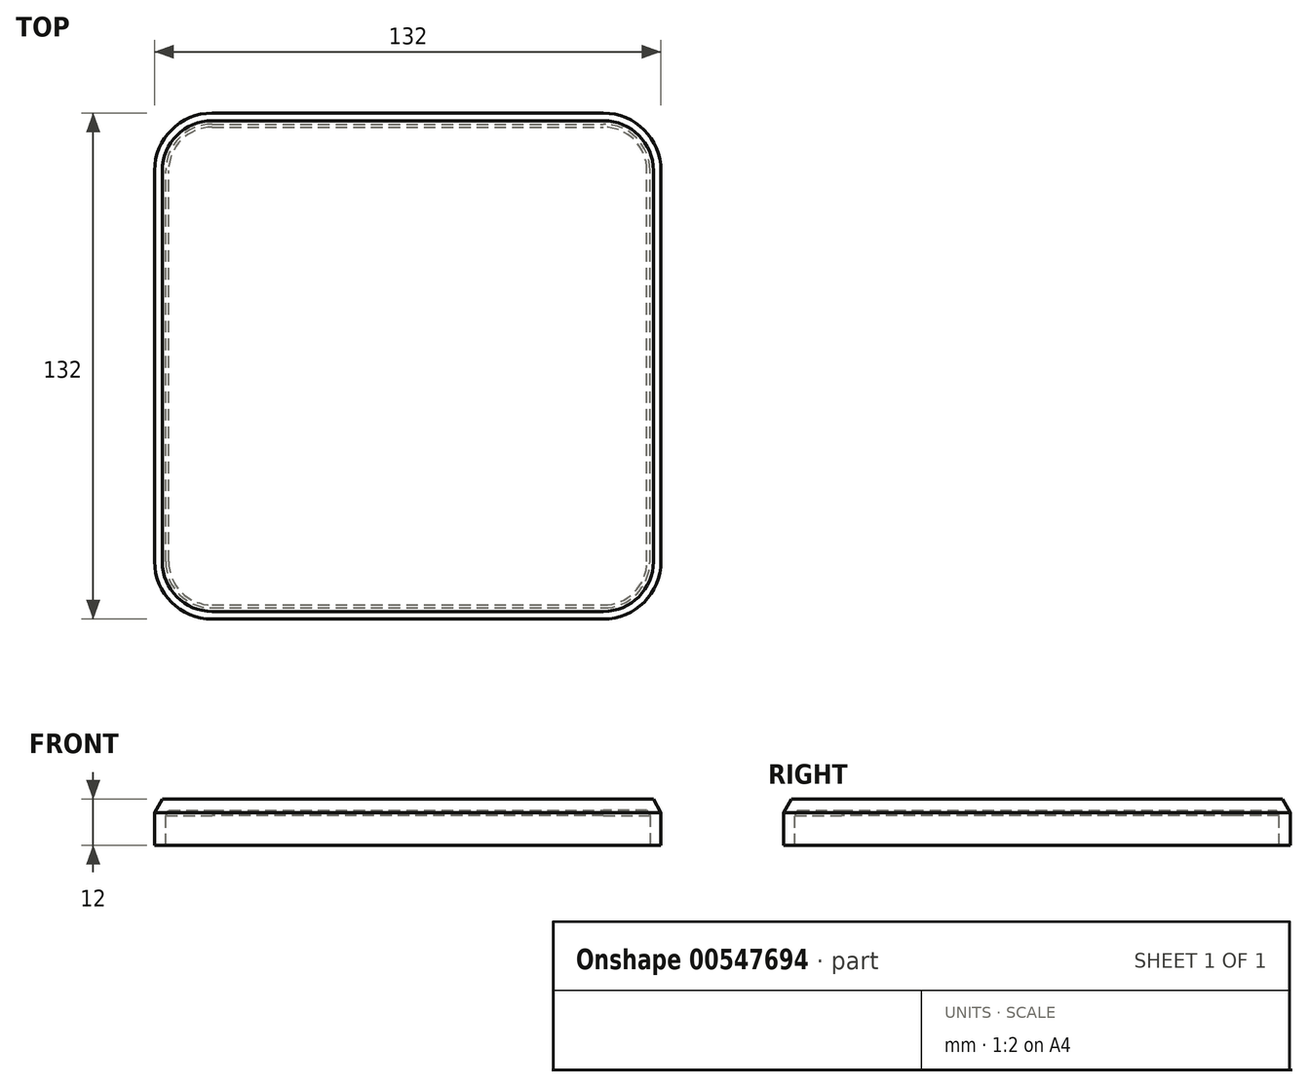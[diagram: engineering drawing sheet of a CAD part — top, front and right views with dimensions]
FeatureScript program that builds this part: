
annotation { "Feature Type Name" : "Feature", "Feature Type Description" : "" }
export const myFeature = defineFeature(function(context is Context, id is Id, definition is map)
    precondition{}
    {
        {
            var Q0;
            Q0=qCreatedBy(makeId("Top.planeOp"),FACE);
            var sketch = newSketch(context, id + "F0", { "sketchPlane" : qUnion([Q0])});
            skLineSegment(sketch, "E0.bottom", {"start": v(-51, -66) * mm, "end": v(51, -66) * mm});
            skLineSegment(sketch, "E0.top", {"start": v(-51, 66) * mm, "end": v(51, 66) * mm});
            skLineSegment(sketch, "E0.left", {"start": v(-66, -51) * mm, "end": v(-66, 51) * mm});
            skLineSegment(sketch, "E0.right", {"start": v(66, -51) * mm, "end": v(66, 51) * mm});
            skPoint(sketch, "E1", {"position": v(-66, 0) * mm});
            skPoint(sketch, "E2", {"position": v(0, 66) * mm});
            skPoint(sketch, "E3.visualSharp", {"position": v(-66, 66) * mm});
            skArc(sketch, "E3.filletArc", {"start": v(-51, 66) * mm, "mid": v(-61.6, 61.6) * mm, "end": v(-66, 51) * mm});
            skPoint(sketch, "E4.visualSharp", {"position": v(66, 66) * mm});
            skArc(sketch, "E4.filletArc", {"start": v(66, 51) * mm, "mid": v(61.6, 61.6) * mm, "end": v(51, 66) * mm});
            skPoint(sketch, "E5.visualSharp", {"position": v(66, -66) * mm});
            skArc(sketch, "E5.filletArc", {"start": v(51, -66) * mm, "mid": v(61.6, -61.6) * mm, "end": v(66, -51) * mm});
            skPoint(sketch, "E6.visualSharp", {"position": v(-66, -66) * mm});
            skArc(sketch, "E6.filletArc", {"start": v(-66, -51) * mm, "mid": v(-61.6, -61.6) * mm, "end": v(-51, -66) * mm});
            skSolve(sketch);
        }
        {
            var Q0;
            Q0=makeQuery(id+"F0.imprint","IMPRINT",FACE,{"disambiguationData":[TD([[makeQuery(id+"F0.imprint","IMPRINT",EDGE,{"derivedFrom":sQuery(id+"F0.wireOp",EDGE,"E0.bottom")}),1.0]])]});
            extrude(context, id + "F1", {"entities" : qUnion([Q0]), "depth" : 12 * mm, "offsetDistance" : 25 * mm});
        }
        {
            var Q0;
            Q0=makeQuery(id+"F1.opExtrude","CAP_EDGE",EDGE,{"disambiguationData":[OSD([sQuery(id+"F0.wireOp",EDGE,"E0.bottom")])],"isStart":false});
            chamfer(context, id + "F2", {"entities" : qUnion([Q0]), "chamferType" : ChamferType.OFFSET_ANGLE, "width" : 2 * mm, "oppositeDirection" : false, "angle" : 60 * degree, "tangentPropagation" : true});
        }
        {
            var Q0;
            Q0=makeQuery(id+"F1.opExtrude","CAP_FACE",FACE,{"disambiguationData":[OSD([sQuery(id+"F0.wireOp",EDGE,"E0.bottom"),sQuery(id+"F0.wireOp",EDGE,"E0.top"),sQuery(id+"F0.wireOp",EDGE,"E0.left"),sQuery(id+"F0.wireOp",EDGE,"E0.right"),sQuery(id+"F0.wireOp",EDGE,"E3.filletArc"),sQuery(id+"F0.wireOp",EDGE,"E4.filletArc"),sQuery(id+"F0.wireOp",EDGE,"E5.filletArc"),sQuery(id+"F0.wireOp",EDGE,"E6.filletArc")])],"isStart":true});
            shell(context, id + "F3", {"entities" : qUnion([Q0]), "thickness" : 2.9 * mm});
        }
    });
